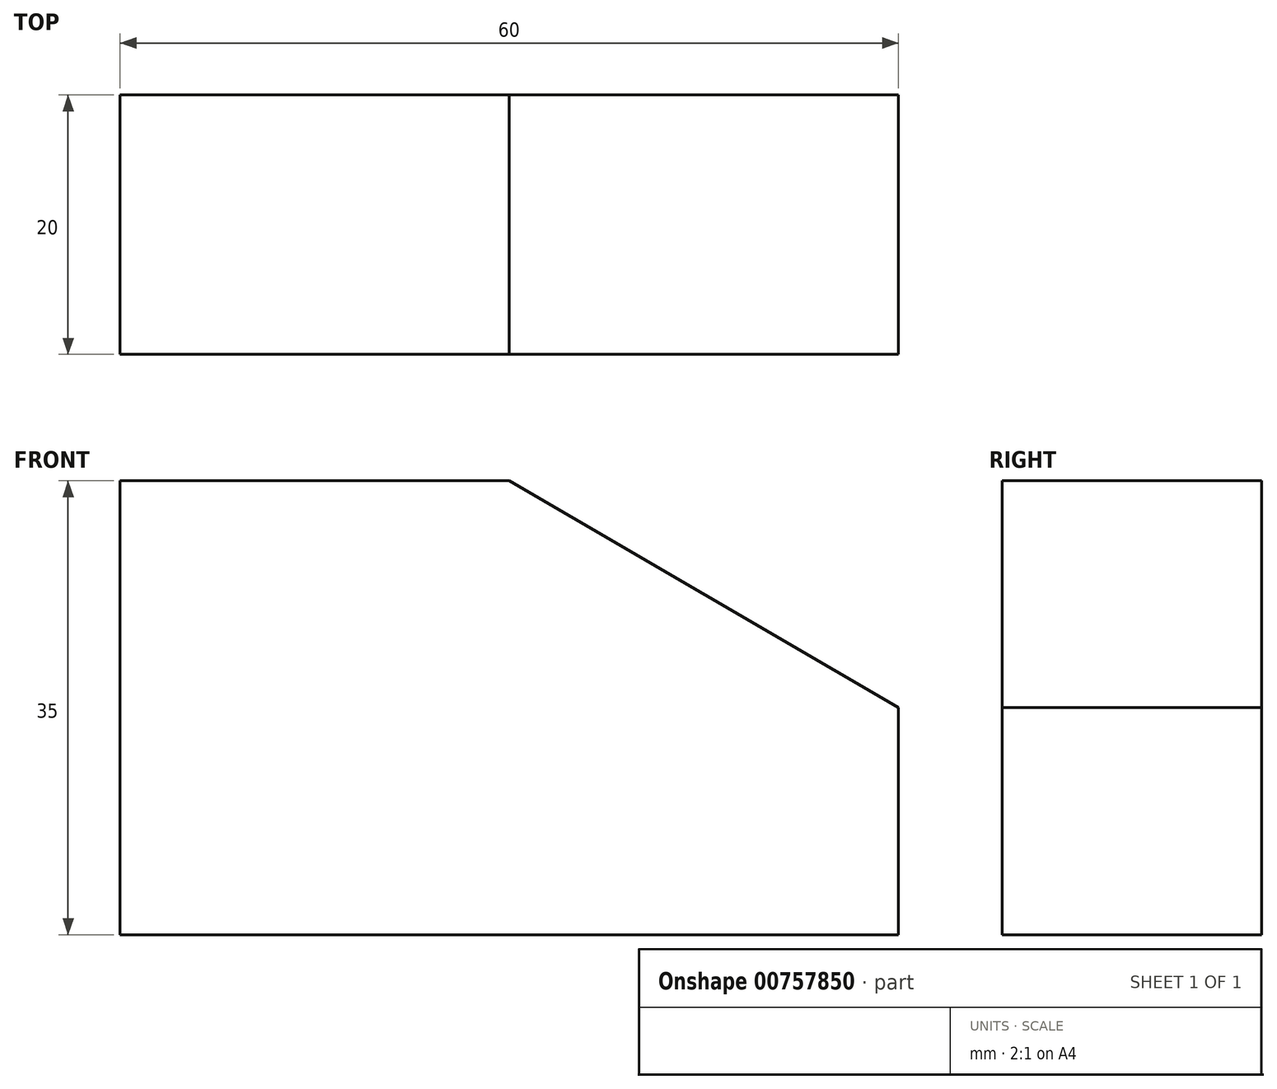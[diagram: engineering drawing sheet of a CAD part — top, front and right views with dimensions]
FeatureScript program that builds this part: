
annotation { "Feature Type Name" : "Feature", "Feature Type Description" : "" }
export const myFeature = defineFeature(function(context is Context, id is Id, definition is map)
    precondition{}
    {
        {
            var Q0;
            Q0=qCreatedBy(makeId("Front.planeOp"),FACE);
            var sketch = newSketch(context, id + "F0", { "sketchPlane" : qUnion([Q0])});
            skLineSegment(sketch, "E0", {"start": v(0, 0) * mm, "end": v(0, 35) * mm});
            skLineSegment(sketch, "E1", {"start": v(0, 35) * mm, "end": v(30, 35) * mm});
            skLineSegment(sketch, "E2", {"start": v(0, 0) * mm, "end": v(60, 0) * mm});
            skLineSegment(sketch, "E3", {"start": v(60, 0) * mm, "end": v(60, 17.5) * mm});
            skLineSegment(sketch, "E4", {"start": v(30, 35) * mm, "end": v(60, 17.5) * mm});
            skSolve(sketch);
        }
        {
            var Q0;
            Q0 = qSketchRegion(id + "F0", true);
            extrude(context, id + "F1", {"entities" : qUnion([Q0]), "depth" : 20 * mm, "offsetDistance" : 25 * mm});
        }
    });
